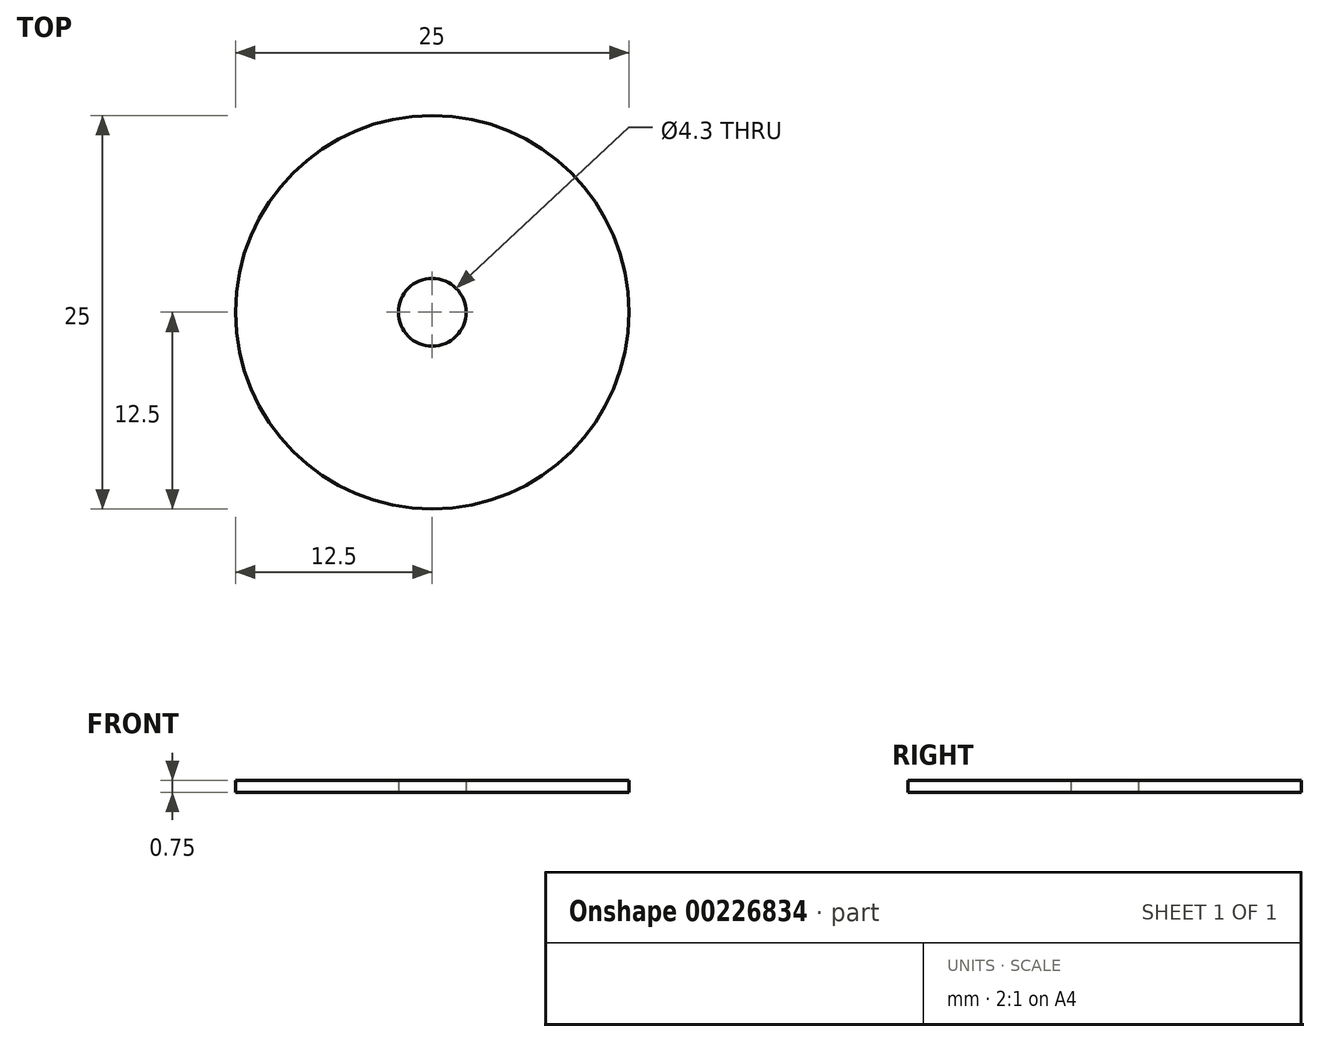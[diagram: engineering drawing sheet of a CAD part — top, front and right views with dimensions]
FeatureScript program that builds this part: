
annotation { "Feature Type Name" : "Feature", "Feature Type Description" : "" }
export const myFeature = defineFeature(function(context is Context, id is Id, definition is map)
    precondition{}
    {
        {
            var Q0;
            Q0=qCreatedBy(makeId("Top.planeOp"),FACE);
            var sketch = newSketch(context, id + "F0", { "sketchPlane" : qUnion([Q0])});
            skCircle(sketch, "E0", {"center": v(0, 0) * mm, "radius": 2.15 * mm});
            skCircle(sketch, "E1", {"center": v(0, 0) * mm, "radius": 12.5 * mm});
            skSolve(sketch);
        }
        {
            var Q0;
            Q0=makeQuery(id+"F0.imprint","IMPRINT",FACE,{"disambiguationData":[TD([[makeQuery(id+"F0.imprint","IMPRINT",EDGE,{"derivedFrom":sQuery(id+"F0.wireOp",EDGE,"E0")}),-1.0]])]});
            extrude(context, id + "F1", {"entities" : qUnion([Q0]), "depth" : .75 * mm});
        }
    });
